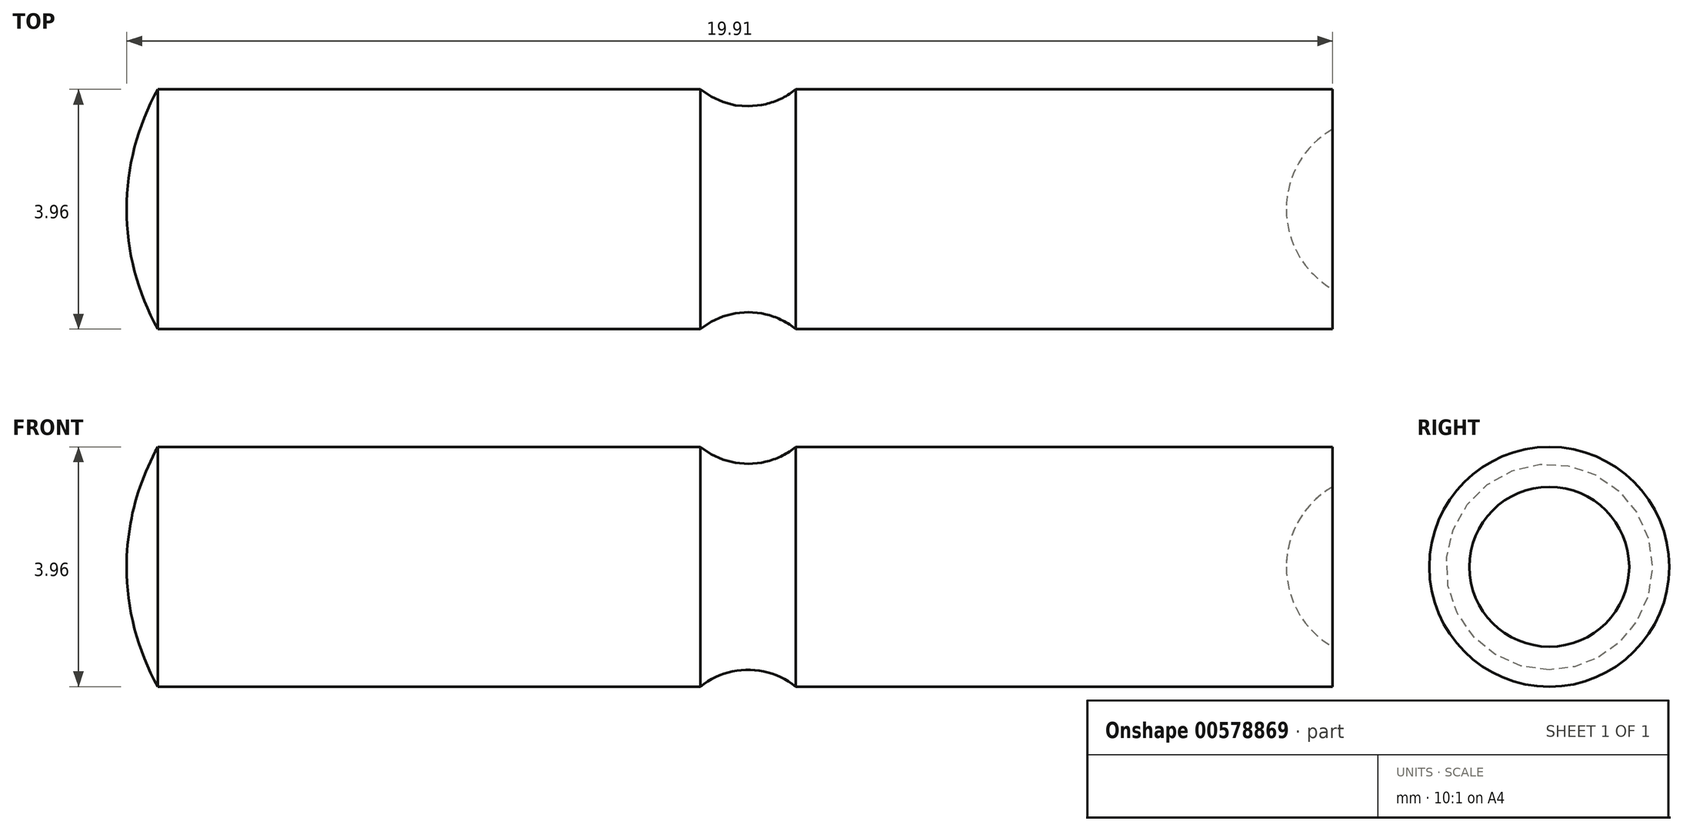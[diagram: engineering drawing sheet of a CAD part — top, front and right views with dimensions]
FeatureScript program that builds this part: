
annotation { "Feature Type Name" : "Feature", "Feature Type Description" : "" }
export const myFeature = defineFeature(function(context is Context, id is Id, definition is map)
    precondition{}
    {
        {
            var Q0;
            Q0=qCreatedBy(makeId("Right.planeOp"),FACE);
            var sketch = newSketch(context, id + "F0", { "sketchPlane" : qUnion([Q0])});
            skCircle(sketch, "E0", {"center": v(0, 0) * mm, "radius": 1.98 * mm});
            skSolve(sketch);
        }
        {
            var Q0;
            Q0=makeQuery(id+"F0.imprint","IMPRINT",FACE,{"disambiguationData":[TD([[makeQuery(id+"F0.imprint","IMPRINT",EDGE,{"derivedFrom":sQuery(id+"F0.wireOp",EDGE,"E0")}),1.0]])]});
            extrude(context, id + "F1", {"entities" : qUnion([Q0]), "endBound" : BoundingType.SYMMETRIC, "depth" : 19.94 * mm});
        }
        {
            var Q0;
            Q0=qCreatedBy(makeId("Front.planeOp"),FACE);
            var sketch = newSketch(context, id + "F2", { "sketchPlane" : qUnion([Q0])});
            skLineSegment(sketch, "E1.0", {"start": v(9.97, 1.32) * mm, "end": v(9.97, 0) * mm});
            skArc(sketch, "E2", {"start": v(9.97, 1.32) * mm, "mid": v(9.41, 0.76) * mm, "end": v(9.2, 0) * mm});
            skPoint(sketch, "E3.orphan", {"position": v(9.97, 1.98) * mm});
            skPoint(sketch, "E4.orphan", {"position": v(9.97, -1.98) * mm});
            skLineSegment(sketch, "E5", {"start": v(9.97, 0) * mm, "end": v(9.2, 0) * mm});
            skPoint(sketch, "E6.orphan", {"position": v(9.97, -1.32) * mm});
            skSolve(sketch);
        }
        {
            var Q0;
            Q0=qSketchRegion(id+"F2",true);
            var Q1;
            Q1=sQuery(id+"F2.wireOp",EDGE,"E5");
            revolve(context, id + "F3", {"operationType" : NewBodyOperationType.REMOVE, "entities" : qUnion([Q0]), "axis" : qUnion([Q1]), "revolveType" : RevolveType.FULL, "oppositeDirection" : true});
        }
        {
            var Q0;
            Q0=qCreatedBy(makeId("Front.planeOp"),FACE);
            var sketch = newSketch(context, id + "F4", { "sketchPlane" : qUnion([Q0])});
            skLineSegment(sketch, "E7", {"start": v(-5.85, 0) * mm, "end": v(5.91, 0) * mm, "construction": true});
            skLineSegment(sketch, "E8.0", {"start": v(9.97, 1.98) * mm, "end": v(9.97, -1.98) * mm, "construction": true});
            skLineSegment(sketch, "E9", {"start": v(-0.47, 1.98) * mm, "end": v(1.1, 1.98) * mm});
            skArc(sketch, "E10", {"start": v(-0.47, 1.98) * mm, "mid": v(0.32, 1.7) * mm, "end": v(1.1, 1.98) * mm});
            skSolve(sketch);
        }
        {
            var Q0;
            Q0=qSketchRegion(id+"F4",true);
            var Q1;
            Q1=sQuery(id+"F4.wireOp",EDGE,"E7");
            revolve(context, id + "F5", {"operationType" : NewBodyOperationType.REMOVE, "entities" : qUnion([Q0]), "axis" : qUnion([Q1]), "revolveType" : RevolveType.FULL, "oppositeDirection" : true});
        }
        {
            var Q0;
            Q0=qCreatedBy(makeId("Front.planeOp"),FACE);
            var sketch = newSketch(context, id + "F6", { "sketchPlane" : qUnion([Q0])});
            skArc(sketch, "E11", {"start": v(-9.43, 1.98) * mm, "mid": v(-9.81, 1.02) * mm, "end": v(-9.94, 0) * mm});
            skLineSegment(sketch, "E12", {"start": v(-9.97, 1.98) * mm, "end": v(-9.43, 1.98) * mm});
            skLineSegment(sketch, "E13.0", {"start": v(-9.97, 1.98) * mm, "end": v(-9.97, 0) * mm});
            skLineSegment(sketch, "E14", {"start": v(-9.97, 0) * mm, "end": v(-9.94, 0) * mm});
            skPoint(sketch, "E15.orphan", {"position": v(-9.97, -1.98) * mm});
            skSolve(sketch);
        }
        {
            var Q0;
            Q0=qSketchRegion(id+"F6",true);
            var Q1;
            Q1=sQuery(id+"F6.wireOp",EDGE,"E14");
            revolve(context, id + "F7", {"operationType" : NewBodyOperationType.REMOVE, "entities" : qUnion([Q0]), "axis" : qUnion([Q1]), "revolveType" : RevolveType.FULL, "oppositeDirection" : true});
        }
    });
